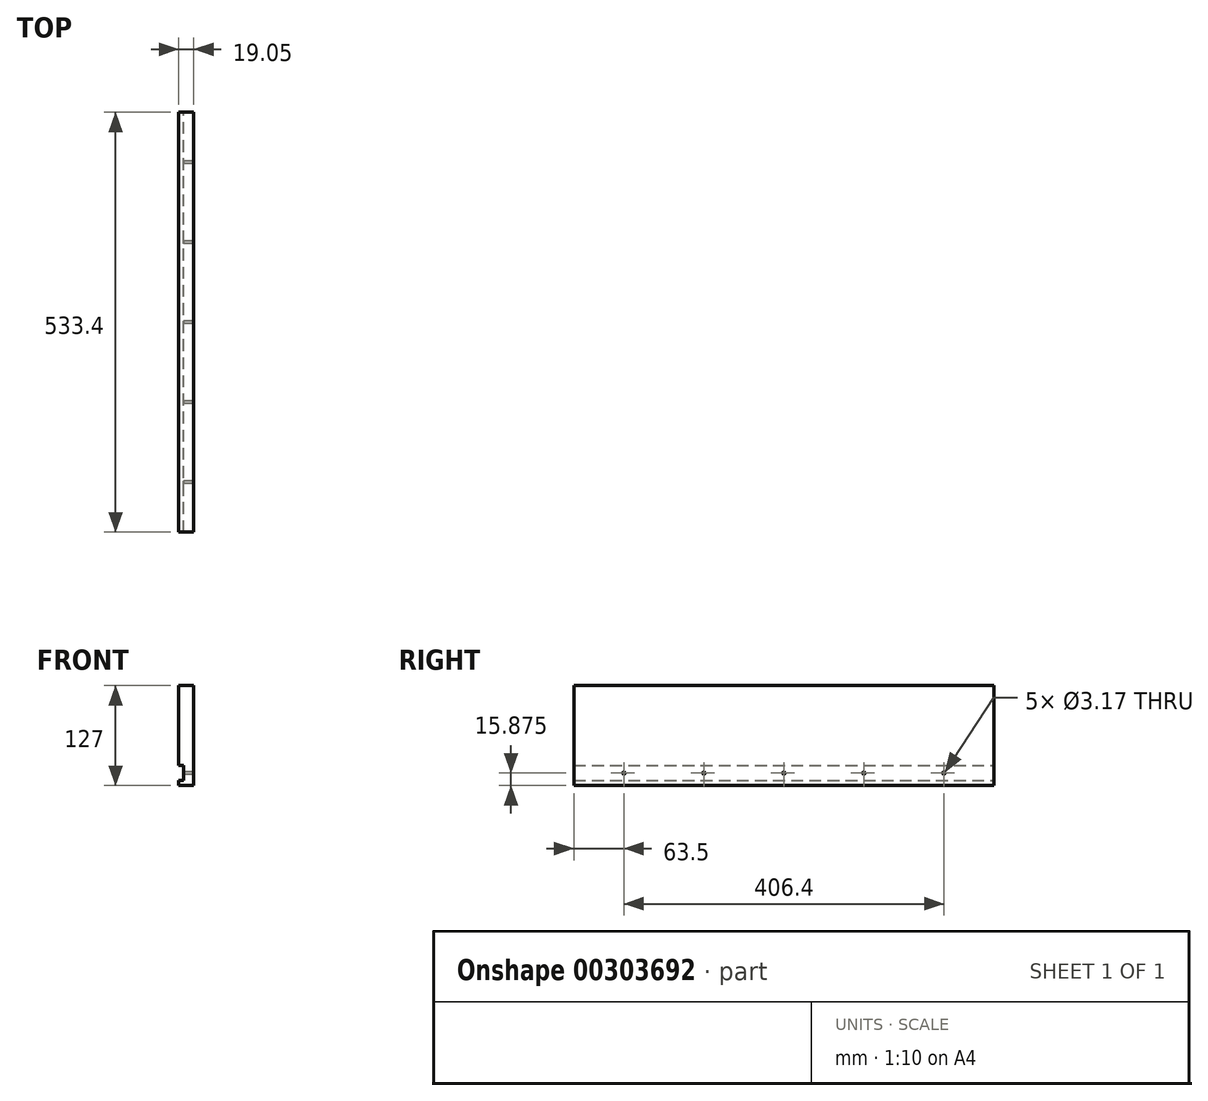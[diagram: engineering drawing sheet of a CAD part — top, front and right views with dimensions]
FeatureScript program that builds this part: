
annotation { "Feature Type Name" : "Feature", "Feature Type Description" : "" }
export const myFeature = defineFeature(function(context is Context, id is Id, definition is map)
    precondition{}
    {
        {
            var Q0;
            Q0=qCreatedBy(makeId("Right.planeOp"),FACE);
            var sketch = newSketch(context, id + "F0", { "sketchPlane" : qUnion([Q0])});
            skLineSegment(sketch, "E0.bottom", {"start": v(0, 0) * mm, "end": v(533.4, 0) * mm});
            skLineSegment(sketch, "E0.top", {"start": v(0, -127) * mm, "end": v(533.4, -127) * mm});
            skLineSegment(sketch, "E0.left", {"start": v(0, 0) * mm, "end": v(0, -127) * mm});
            skLineSegment(sketch, "E0.right", {"start": v(533.4, 0) * mm, "end": v(533.4, -127) * mm});
            skSolve(sketch);
        }
        {
            var Q0;
            Q0 = qSketchRegion(id + "F0", true);
            extrude(context, id + "F1", {"entities" : qUnion([Q0]), "depth" : 19.05 * mm});
        }
        {
            var Q0;
            Q0=qCreatedBy(makeId("Right.planeOp"),FACE);
            var sketch = newSketch(context, id + "F2", { "sketchPlane" : qUnion([Q0])});
            skLineSegment(sketch, "E1.bottom", {"start": v(0, -101.6) * mm, "end": v(533.4, -101.6) * mm});
            skLineSegment(sketch, "E1.top", {"start": v(0, -120.65) * mm, "end": v(533.4, -120.65) * mm});
            skLineSegment(sketch, "E1.left", {"start": v(0, -101.6) * mm, "end": v(0, -120.65) * mm});
            skLineSegment(sketch, "E1.right", {"start": v(533.4, -101.6) * mm, "end": v(533.4, -120.65) * mm});
            skSolve(sketch);
        }
        {
            var Q0;
            Q0 = qSketchRegion(id + "F2", true);
            extrude(context, id + "F3", {"entities" : qUnion([Q0]), "operationType" : NewBodyOperationType.REMOVE, "depth" : 6.35 * mm});
        }
        {
            var Q0;
            Q0=qCreatedBy(makeId("Right.planeOp"),FACE);
            var sketch = newSketch(context, id + "F4", { "sketchPlane" : qUnion([Q0])});
            skCircle(sketch, "E2", {"center": v(469.9, -111.12) * mm, "radius": 1.59 * mm});
            skCircle(sketch, "E3.1.0.0", {"center": v(368.3, -111.12) * mm, "radius": 1.59 * mm});
            skCircle(sketch, "E3.2.0.0", {"center": v(266.7, -111.12) * mm, "radius": 1.59 * mm});
            skCircle(sketch, "E3.3.0.0", {"center": v(165.1, -111.12) * mm, "radius": 1.59 * mm});
            skCircle(sketch, "E3.4.0.0", {"center": v(63.5, -111.12) * mm, "radius": 1.59 * mm});
            skLineSegment(sketch, "E3.direction1", {"start": v(469.9, -111.12) * mm, "end": v(368.3, -111.12) * mm, "construction": true});
            skSolve(sketch);
        }
        {
            var Q0;
            Q0 = qSketchRegion(id + "F4", true);
            extrude(context, id + "F5", {"entities" : qUnion([Q0]), "operationType" : NewBodyOperationType.REMOVE, "endBound" : BoundingType.THROUGH_ALL, "depth" : 25.4 * mm});
        }
    });
